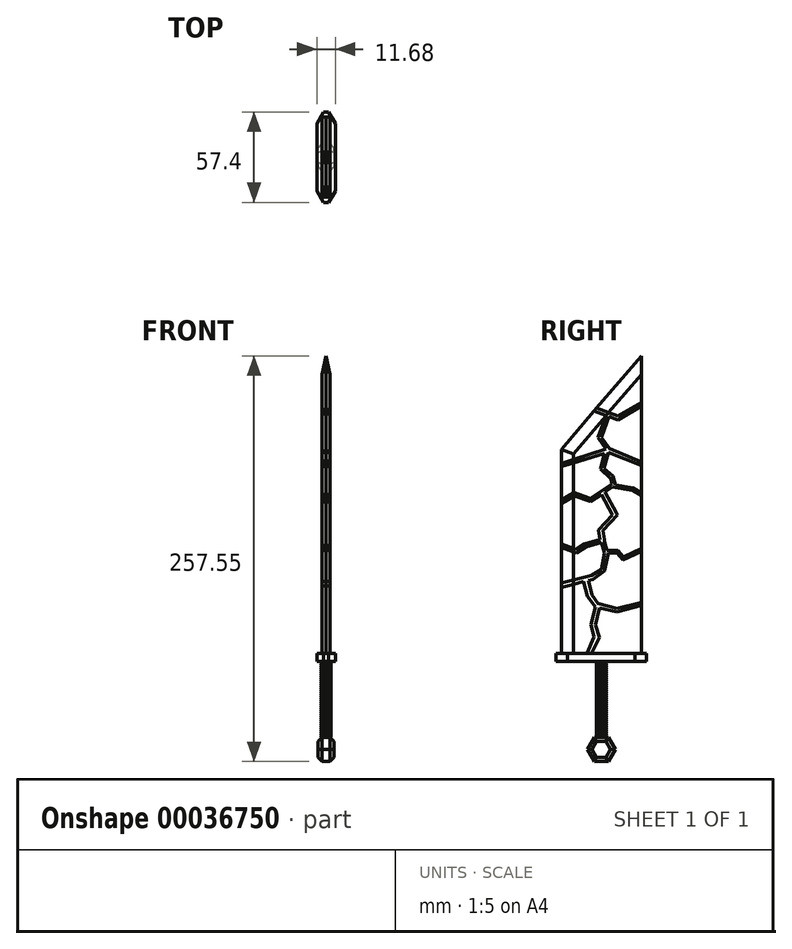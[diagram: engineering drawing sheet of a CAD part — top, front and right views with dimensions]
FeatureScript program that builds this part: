
annotation { "Feature Type Name" : "Feature", "Feature Type Description" : "" }
export const myFeature = defineFeature(function(context is Context, id is Id, definition is map)
    precondition{}
    {
        {
            var Q0;
            Q0=qCreatedBy(makeId("Right.planeOp"),FACE);
            var sketch = newSketch(context, id + "F0", { "sketchPlane" : qUnion([Q0])});
            skLineSegment(sketch, "E0", {"start": v(-25.4, 41.33) * mm, "end": v(-25.4, 83.27) * mm});
            skLineSegment(sketch, "E1", {"start": v(25.4, 41.33) * mm, "end": v(25.4, 71.64) * mm});
            skLineSegment(sketch, "E2", {"start": v(25.4, 171.08) * mm, "end": v(25.4, 198.27) * mm});
            skLineSegment(sketch, "E3", {"start": v(25.4, 230.2) * mm, "end": v(-2.99, 197.01) * mm});
            skLineSegment(sketch, "E4", {"start": v(25.4, 200.64) * mm, "end": v(10.42, 191.99) * mm});
            skLineSegment(sketch, "E5", {"start": v(25.4, 198.27) * mm, "end": v(10.42, 189.63) * mm});
            skLineSegment(sketch, "E6", {"start": v(10.42, 191.99) * mm, "end": v(-2.99, 197.01) * mm});
            skLineSegment(sketch, "E7", {"start": v(10.42, 189.63) * mm, "end": v(4.82, 191.68) * mm});
            skLineSegment(sketch, "E8.trimOffspring", {"start": v(-4.6, 195.13) * mm, "end": v(-25.4, 170.8) * mm});
            skLineSegment(sketch, "E9.trimOffspring", {"start": v(25.4, 200.64) * mm, "end": v(25.4, 230.2) * mm});
            skLineSegment(sketch, "E10", {"start": v(2.91, 192.38) * mm, "end": v(-2.2, 178.46) * mm});
            skLineSegment(sketch, "E11", {"start": v(-2.2, 178.46) * mm, "end": v(2.98, 171.03) * mm});
            skLineSegment(sketch, "E12", {"start": v(4.45, 168.92) * mm, "end": v(25.4, 160.6) * mm});
            skLineSegment(sketch, "E13", {"start": v(4.82, 191.68) * mm, "end": v(0, 178.53) * mm});
            skLineSegment(sketch, "E14", {"start": v(0, 178.53) * mm, "end": v(5, 171.35) * mm});
            skLineSegment(sketch, "E15", {"start": v(5, 171.35) * mm, "end": v(25.4, 162.82) * mm});
            skPoint(sketch, "E16.end.orphan", {"position": v(25.4, 162.82) * mm});
            skLineSegment(sketch, "E17.trimOffspring", {"start": v(25.4, 162.82) * mm, "end": v(25.4, 171.08) * mm});
            skLineSegment(sketch, "E18.trimOffspring", {"start": v(2.91, 192.38) * mm, "end": v(-4.6, 195.13) * mm});
            skLineSegment(sketch, "E19", {"start": v(1.83, 168.13) * mm, "end": v(-25.4, 159.9) * mm});
            skLineSegment(sketch, "E20", {"start": v(2.98, 171.03) * mm, "end": v(-25.4, 161.87) * mm});
            skLineSegment(sketch, "E21.trimOffspring", {"start": v(-25.4, 161.87) * mm, "end": v(-25.4, 170.8) * mm});
            skLineSegment(sketch, "E22", {"start": v(1.83, 168.13) * mm, "end": v(-0.65, 158.4) * mm});
            skLineSegment(sketch, "E23", {"start": v(-0.65, 158.4) * mm, "end": v(6.14, 152.23) * mm});
            skLineSegment(sketch, "E24", {"start": v(6.14, 152.23) * mm, "end": v(6.68, 148.9) * mm});
            skLineSegment(sketch, "E25", {"start": v(7, 146.87) * mm, "end": v(20.03, 144.9) * mm});
            skLineSegment(sketch, "E26", {"start": v(20.03, 144.9) * mm, "end": v(25.4, 141.55) * mm});
            skLineSegment(sketch, "E27", {"start": v(4.45, 168.92) * mm, "end": v(1.56, 158.78) * mm});
            skLineSegment(sketch, "E28", {"start": v(1.56, 158.78) * mm, "end": v(7.43, 153.9) * mm});
            skLineSegment(sketch, "E29", {"start": v(7.43, 153.9) * mm, "end": v(8.95, 148.23) * mm});
            skLineSegment(sketch, "E30", {"start": v(8.95, 148.23) * mm, "end": v(20.11, 146.47) * mm});
            skLineSegment(sketch, "E31", {"start": v(20.11, 146.47) * mm, "end": v(25.4, 143.2) * mm});
            skLineSegment(sketch, "E32.trimOffspring", {"start": v(25.4, 143.2) * mm, "end": v(25.4, 160.6) * mm});
            skLineSegment(sketch, "E33", {"start": v(7, 146.87) * mm, "end": v(2.24, 143.71) * mm});
            skLineSegment(sketch, "E34", {"start": v(-6.87, 137.68) * mm, "end": v(-17.21, 141.33) * mm});
            skLineSegment(sketch, "E35", {"start": v(-17.21, 141.33) * mm, "end": v(-25.4, 136.67) * mm});
            skLineSegment(sketch, "E36", {"start": v(6.68, 148.9) * mm, "end": v(-7.04, 139.82) * mm});
            skLineSegment(sketch, "E37", {"start": v(-7.04, 139.82) * mm, "end": v(-17.31, 143.56) * mm});
            skLineSegment(sketch, "E38", {"start": v(-17.31, 143.56) * mm, "end": v(-25.4, 138.7) * mm});
            skLineSegment(sketch, "E39.trimOffspring", {"start": v(-25.4, 138.7) * mm, "end": v(-25.4, 159.9) * mm});
            skLineSegment(sketch, "E40", {"start": v(-25.4, 41.33) * mm, "end": v(25.4, 41.33) * mm});
            skLineSegment(sketch, "E41", {"start": v(0.07, 142.27) * mm, "end": v(7.1, 129.29) * mm});
            skLineSegment(sketch, "E42", {"start": v(7.1, 129.29) * mm, "end": v(-1.77, 119.78) * mm});
            skLineSegment(sketch, "E43", {"start": v(-1.77, 119.78) * mm, "end": v(-0.97, 113.72) * mm});
            skLineSegment(sketch, "E44", {"start": v(-0.97, 113.72) * mm, "end": v(-10.63, 110.68) * mm});
            skLineSegment(sketch, "E45", {"start": v(-10.63, 110.68) * mm, "end": v(-16.14, 107.25) * mm});
            skLineSegment(sketch, "E46", {"start": v(-16.14, 107.25) * mm, "end": v(-25.4, 110.92) * mm});
            skLineSegment(sketch, "E47", {"start": v(2.24, 143.71) * mm, "end": v(9.57, 130.56) * mm});
            skLineSegment(sketch, "E48", {"start": v(9.57, 130.56) * mm, "end": v(10.37, 129.13) * mm});
            skLineSegment(sketch, "E49", {"start": v(10.37, 129.13) * mm, "end": v(1.03, 119.3) * mm});
            skLineSegment(sketch, "E50", {"start": v(1.03, 119.3) * mm, "end": v(1.99, 113.8) * mm});
            skLineSegment(sketch, "E51", {"start": v(1.99, 113.8) * mm, "end": v(1.99, 112.36) * mm});
            skLineSegment(sketch, "E52", {"start": v(0, 111.77) * mm, "end": v(-9.83, 108.85) * mm});
            skLineSegment(sketch, "E53", {"start": v(-9.83, 108.85) * mm, "end": v(-15.9, 105.17) * mm});
            skLineSegment(sketch, "E54", {"start": v(-15.9, 105.17) * mm, "end": v(-25.4, 108.45) * mm});
            skLineSegment(sketch, "E55", {"start": v(1.99, 112.36) * mm, "end": v(3.64, 106.8) * mm});
            skLineSegment(sketch, "E56", {"start": v(3.64, 106.8) * mm, "end": v(10.53, 106.8) * mm});
            skLineSegment(sketch, "E57", {"start": v(10.53, 106.8) * mm, "end": v(13.96, 102.7) * mm});
            skLineSegment(sketch, "E58", {"start": v(13.96, 102.7) * mm, "end": v(25.4, 107.97) * mm});
            skLineSegment(sketch, "E59", {"start": v(0, 111.77) * mm, "end": v(1.99, 105.08) * mm});
            skLineSegment(sketch, "E60", {"start": v(9.76, 105.08) * mm, "end": v(13.86, 100.53) * mm});
            skLineSegment(sketch, "E61", {"start": v(13.86, 100.53) * mm, "end": v(25.4, 105.97) * mm});
            skLineSegment(sketch, "E62.trimOffspring", {"start": v(-25.4, 110.92) * mm, "end": v(-25.4, 136.67) * mm});
            skLineSegment(sketch, "E63.trimOffspring", {"start": v(25.4, 107.97) * mm, "end": v(25.4, 141.55) * mm});
            skLineSegment(sketch, "E64.trimOffspring", {"start": v(0.07, 142.27) * mm, "end": v(-6.87, 137.68) * mm});
            skLineSegment(sketch, "E65", {"start": v(1.99, 105.08) * mm, "end": v(0, 94.48) * mm});
            skLineSegment(sketch, "E66", {"start": v(0, 94.48) * mm, "end": v(-6.17, 90.77) * mm});
            skLineSegment(sketch, "E67", {"start": v(-6.17, 90.77) * mm, "end": v(-25.4, 85.94) * mm});
            skLineSegment(sketch, "E68", {"start": v(4.63, 105.08) * mm, "end": v(1.99, 93.55) * mm});
            skLineSegment(sketch, "E69", {"start": v(1.99, 93.55) * mm, "end": v(-5.45, 88.3) * mm});
            skLineSegment(sketch, "E70", {"start": v(-5.45, 88.3) * mm, "end": v(-8.14, 87.63) * mm});
            skLineSegment(sketch, "E71", {"start": v(-11.26, 86.84) * mm, "end": v(-8.9, 77.54) * mm});
            skLineSegment(sketch, "E72", {"start": v(-8.9, 77.54) * mm, "end": v(-3.9, 70.92) * mm});
            skLineSegment(sketch, "E73", {"start": v(-1.28, 70.3) * mm, "end": v(9.87, 67.63) * mm});
            skLineSegment(sketch, "E74", {"start": v(9.87, 67.63) * mm, "end": v(25.4, 71.64) * mm});
            skLineSegment(sketch, "E75", {"start": v(-8.14, 87.63) * mm, "end": v(-5.84, 78.54) * mm});
            skLineSegment(sketch, "E76", {"start": v(-5.84, 78.54) * mm, "end": v(-2.06, 73.08) * mm});
            skLineSegment(sketch, "E77", {"start": v(-2.06, 73.08) * mm, "end": v(9.77, 69.7) * mm});
            skLineSegment(sketch, "E78", {"start": v(9.77, 69.7) * mm, "end": v(25.4, 73.65) * mm});
            skLineSegment(sketch, "E79.trimOffspring", {"start": v(-11.26, 86.84) * mm, "end": v(-25.4, 83.27) * mm});
            skLineSegment(sketch, "E80.trimOffspring", {"start": v(-25.4, 85.94) * mm, "end": v(-25.4, 108.45) * mm});
            skLineSegment(sketch, "E81.trimOffspring", {"start": v(25.4, 73.65) * mm, "end": v(25.4, 105.97) * mm});
            skLineSegment(sketch, "E82", {"start": v(4.63, 105.08) * mm, "end": v(9.76, 105.08) * mm});
            skLineSegment(sketch, "E83", {"start": v(-3.9, 70.92) * mm, "end": v(-6.61, 59.6) * mm});
            skLineSegment(sketch, "E84", {"start": v(-6.61, 59.6) * mm, "end": v(-4.58, 51.74) * mm});
            skLineSegment(sketch, "E85", {"start": v(-4.58, 51.74) * mm, "end": v(-9.16, 41.33) * mm});
            skLineSegment(sketch, "E86", {"start": v(-1.28, 70.3) * mm, "end": v(-3.87, 59.47) * mm});
            skLineSegment(sketch, "E87", {"start": v(-3.87, 59.47) * mm, "end": v(-1.11, 51.4) * mm});
            skLineSegment(sketch, "E88", {"start": v(-1.11, 51.4) * mm, "end": v(-6.37, 41.33) * mm});
            skSolve(sketch);
        }
        {
            var Q0;
            Q0 = qSketchRegion(id + "F0", true);
            extrude(context, id + "F1", {"entities" : qUnion([Q0]), "endBound" : BoundingType.SYMMETRIC, "depth" : 5.08 * mm});
        }
        {
            var Q0;
            Q0=qCreatedBy(makeId("Right.planeOp"),FACE);
            var sketch = newSketch(context, id + "F2", { "sketchPlane" : qUnion([Q0])});
            skLineSegment(sketch, "E89.0", {"start": v(2.91, 192.38) * mm, "end": v(-4.6, 195.13) * mm});
            skLineSegment(sketch, "E90.0", {"start": v(10.42, 191.99) * mm, "end": v(-2.99, 197.01) * mm});
            skLineSegment(sketch, "E91.0", {"start": v(10.42, 189.63) * mm, "end": v(4.82, 191.68) * mm});
            skLineSegment(sketch, "E92.0", {"start": v(25.4, 198.27) * mm, "end": v(10.42, 189.63) * mm});
            skLineSegment(sketch, "E93.0", {"start": v(25.4, 200.64) * mm, "end": v(10.42, 191.99) * mm});
            skLineSegment(sketch, "E94.0", {"start": v(4.82, 191.68) * mm, "end": v(0, 178.53) * mm});
            skLineSegment(sketch, "E95.0", {"start": v(2.91, 192.38) * mm, "end": v(-2.2, 178.46) * mm});
            skLineSegment(sketch, "E96.0", {"start": v(-2.2, 178.46) * mm, "end": v(2.98, 171.03) * mm});
            skLineSegment(sketch, "E97.0", {"start": v(0, 178.53) * mm, "end": v(5, 171.35) * mm});
            skLineSegment(sketch, "E98.0", {"start": v(5, 171.35) * mm, "end": v(25.4, 162.82) * mm});
            skLineSegment(sketch, "E99.0", {"start": v(4.45, 168.92) * mm, "end": v(25.4, 160.6) * mm});
            skLineSegment(sketch, "E100.0", {"start": v(2.98, 171.03) * mm, "end": v(-25.4, 161.87) * mm});
            skLineSegment(sketch, "E101.0", {"start": v(1.83, 168.13) * mm, "end": v(-0.65, 158.4) * mm});
            skLineSegment(sketch, "E102.0", {"start": v(4.45, 168.92) * mm, "end": v(1.56, 158.78) * mm});
            skLineSegment(sketch, "E103.0", {"start": v(-0.65, 158.4) * mm, "end": v(6.14, 152.23) * mm});
            skLineSegment(sketch, "E104.0", {"start": v(1.56, 158.78) * mm, "end": v(7.43, 153.9) * mm});
            skLineSegment(sketch, "E105.0", {"start": v(7.43, 153.9) * mm, "end": v(8.95, 148.23) * mm});
            skLineSegment(sketch, "E106.0", {"start": v(6.14, 152.23) * mm, "end": v(6.68, 148.9) * mm});
            skLineSegment(sketch, "E107.0", {"start": v(8.95, 148.23) * mm, "end": v(20.11, 146.47) * mm});
            skLineSegment(sketch, "E108.0", {"start": v(20.11, 146.47) * mm, "end": v(25.4, 143.2) * mm});
            skLineSegment(sketch, "E109.0", {"start": v(20.03, 144.9) * mm, "end": v(25.4, 141.55) * mm});
            skLineSegment(sketch, "E110.0", {"start": v(7, 146.87) * mm, "end": v(20.03, 144.9) * mm});
            skLineSegment(sketch, "E111.0", {"start": v(6.68, 148.9) * mm, "end": v(-7.04, 139.82) * mm});
            skLineSegment(sketch, "E112.0", {"start": v(7, 146.87) * mm, "end": v(2.24, 143.71) * mm});
            skLineSegment(sketch, "E113.0", {"start": v(-17.31, 143.56) * mm, "end": v(-25.4, 138.7) * mm});
            skLineSegment(sketch, "E114.0", {"start": v(-17.21, 141.33) * mm, "end": v(-25.4, 136.67) * mm});
            skLineSegment(sketch, "E115.0", {"start": v(-7.04, 139.82) * mm, "end": v(-17.31, 143.56) * mm});
            skLineSegment(sketch, "E116.0", {"start": v(-6.87, 137.68) * mm, "end": v(-17.21, 141.33) * mm});
            skLineSegment(sketch, "E117.0", {"start": v(0.07, 142.27) * mm, "end": v(-6.87, 137.68) * mm});
            skLineSegment(sketch, "E118.0", {"start": v(0.07, 142.27) * mm, "end": v(7.1, 129.29) * mm});
            skLineSegment(sketch, "E119.0", {"start": v(2.24, 143.71) * mm, "end": v(9.57, 130.56) * mm});
            skLineSegment(sketch, "E120.0", {"start": v(9.57, 130.56) * mm, "end": v(10.37, 129.13) * mm});
            skLineSegment(sketch, "E121.0", {"start": v(10.37, 129.13) * mm, "end": v(1.03, 119.3) * mm});
            skLineSegment(sketch, "E122.0", {"start": v(7.1, 129.29) * mm, "end": v(-1.77, 119.78) * mm});
            skLineSegment(sketch, "E123.0", {"start": v(-1.77, 119.78) * mm, "end": v(-0.97, 113.72) * mm});
            skLineSegment(sketch, "E124.0", {"start": v(1.03, 119.3) * mm, "end": v(1.99, 113.8) * mm});
            skLineSegment(sketch, "E125.0", {"start": v(1.99, 113.8) * mm, "end": v(1.99, 112.36) * mm});
            skLineSegment(sketch, "E126.0", {"start": v(1.99, 112.36) * mm, "end": v(3.64, 106.8) * mm});
            skLineSegment(sketch, "E127.0", {"start": v(0, 111.77) * mm, "end": v(1.99, 105.08) * mm});
            skLineSegment(sketch, "E128.0", {"start": v(-0.97, 113.72) * mm, "end": v(-10.63, 110.68) * mm});
            skLineSegment(sketch, "E129.0", {"start": v(-10.63, 110.68) * mm, "end": v(-16.14, 107.25) * mm});
            skLineSegment(sketch, "E130.0", {"start": v(-16.14, 107.25) * mm, "end": v(-25.4, 110.92) * mm});
            skLineSegment(sketch, "E131.0", {"start": v(-15.9, 105.17) * mm, "end": v(-25.4, 108.45) * mm});
            skLineSegment(sketch, "E132.0", {"start": v(-9.83, 108.85) * mm, "end": v(-15.9, 105.17) * mm});
            skLineSegment(sketch, "E133.0", {"start": v(0, 111.77) * mm, "end": v(-9.83, 108.85) * mm});
            skLineSegment(sketch, "E134.0", {"start": v(3.64, 106.8) * mm, "end": v(10.53, 106.8) * mm});
            skLineSegment(sketch, "E135.0", {"start": v(4.63, 105.08) * mm, "end": v(9.76, 105.08) * mm});
            skLineSegment(sketch, "E136.0", {"start": v(9.76, 105.08) * mm, "end": v(13.86, 100.53) * mm});
            skLineSegment(sketch, "E137.0", {"start": v(10.53, 106.8) * mm, "end": v(13.96, 102.7) * mm});
            skLineSegment(sketch, "E138.0", {"start": v(13.96, 102.7) * mm, "end": v(25.4, 107.97) * mm});
            skLineSegment(sketch, "E139.0", {"start": v(13.86, 100.53) * mm, "end": v(25.4, 105.97) * mm});
            skLineSegment(sketch, "E140.0", {"start": v(1.99, 105.08) * mm, "end": v(0, 94.48) * mm});
            skLineSegment(sketch, "E141.0", {"start": v(4.63, 105.08) * mm, "end": v(1.99, 93.55) * mm});
            skLineSegment(sketch, "E142.0", {"start": v(0, 94.48) * mm, "end": v(-6.17, 90.77) * mm});
            skLineSegment(sketch, "E143.0", {"start": v(-6.17, 90.77) * mm, "end": v(-25.4, 85.94) * mm});
            skLineSegment(sketch, "E144.0", {"start": v(1.99, 93.55) * mm, "end": v(-5.45, 88.3) * mm});
            skLineSegment(sketch, "E145.0", {"start": v(-5.45, 88.3) * mm, "end": v(-8.14, 87.63) * mm});
            skLineSegment(sketch, "E146.0", {"start": v(-11.26, 86.84) * mm, "end": v(-25.4, 83.27) * mm});
            skLineSegment(sketch, "E147.0", {"start": v(-11.26, 86.84) * mm, "end": v(-8.9, 77.54) * mm});
            skLineSegment(sketch, "E148.0", {"start": v(-8.14, 87.63) * mm, "end": v(-5.84, 78.54) * mm});
            skLineSegment(sketch, "E149.0", {"start": v(-5.84, 78.54) * mm, "end": v(-2.06, 73.08) * mm});
            skLineSegment(sketch, "E150.0", {"start": v(-8.9, 77.54) * mm, "end": v(-3.9, 70.92) * mm});
            skLineSegment(sketch, "E151.0", {"start": v(-2.06, 73.08) * mm, "end": v(9.77, 69.7) * mm});
            skLineSegment(sketch, "E152.0", {"start": v(9.77, 69.7) * mm, "end": v(25.4, 73.65) * mm});
            skLineSegment(sketch, "E153.0", {"start": v(9.87, 67.63) * mm, "end": v(25.4, 71.64) * mm});
            skLineSegment(sketch, "E154.0", {"start": v(-1.28, 70.3) * mm, "end": v(9.87, 67.63) * mm});
            skLineSegment(sketch, "E155.0", {"start": v(-3.9, 70.92) * mm, "end": v(-6.61, 59.6) * mm});
            skLineSegment(sketch, "E156.0", {"start": v(-1.28, 70.3) * mm, "end": v(-3.87, 59.47) * mm});
            skLineSegment(sketch, "E157.0", {"start": v(-3.87, 59.47) * mm, "end": v(-1.11, 51.4) * mm});
            skLineSegment(sketch, "E158.0", {"start": v(-6.61, 59.6) * mm, "end": v(-4.58, 51.74) * mm});
            skLineSegment(sketch, "E159.0", {"start": v(-1.11, 51.4) * mm, "end": v(-6.37, 41.33) * mm});
            skLineSegment(sketch, "E160.0", {"start": v(-4.58, 51.74) * mm, "end": v(-9.16, 41.33) * mm});
            skLineSegment(sketch, "E161", {"start": v(-9.16, 41.33) * mm, "end": v(-6.37, 41.33) * mm});
            skLineSegment(sketch, "E162", {"start": v(-25.4, 85.94) * mm, "end": v(-25.4, 83.27) * mm});
            skLineSegment(sketch, "E163", {"start": v(-25.4, 108.45) * mm, "end": v(-25.4, 110.92) * mm});
            skLineSegment(sketch, "E164", {"start": v(-25.4, 138.7) * mm, "end": v(-25.4, 136.67) * mm});
            skLineSegment(sketch, "E165", {"start": v(-25.4, 161.87) * mm, "end": v(-25.4, 159.92) * mm});
            skLineSegment(sketch, "E166", {"start": v(-25.4, 159.92) * mm, "end": v(-25.4, 161.87) * mm});
            skLineSegment(sketch, "E167", {"start": v(-4.6, 195.13) * mm, "end": v(-2.99, 197.01) * mm});
            skLineSegment(sketch, "E168", {"start": v(25.4, 198.27) * mm, "end": v(25.4, 200.64) * mm});
            skLineSegment(sketch, "E169", {"start": v(25.4, 162.82) * mm, "end": v(25.4, 160.6) * mm});
            skLineSegment(sketch, "E170", {"start": v(25.4, 143.2) * mm, "end": v(25.4, 141.55) * mm});
            skLineSegment(sketch, "E171", {"start": v(25.4, 107.97) * mm, "end": v(25.4, 105.97) * mm});
            skLineSegment(sketch, "E172", {"start": v(25.4, 73.65) * mm, "end": v(25.4, 71.64) * mm});
            skLineSegment(sketch, "E173", {"start": v(-25.4, 161.87) * mm, "end": v(2.98, 171.03) * mm});
            skLineSegment(sketch, "E174", {"start": v(-25.4, 159.92) * mm, "end": v(1.83, 168.13) * mm});
            skSolve(sketch);
        }
        {
            var Q0;
            Q0 = qSketchRegion(id + "F2", true);
            extrude(context, id + "F3", {"entities" : qUnion([Q0]), "endBound" : BoundingType.SYMMETRIC, "depth" : 5.08 * mm});
        }
        {
            var Q0;
            Q0=makeQuery(id+"F1.opExtrude","CAP_EDGE",EDGE,{"disambiguationData":[OSD([sQuery(id+"F0.wireOp",EDGE,"E8.trimOffspring")])],"isStart":true});
            var Q1;
            Q1=makeQuery(id+"F1.opExtrude","CAP_EDGE",EDGE,{"disambiguationData":[OSD([sQuery(id+"F0.wireOp",EDGE,"E8.trimOffspring")])],"isStart":false});
            var Q2;
            Q2=makeQuery(id+"F1.opExtrude","CAP_EDGE",EDGE,{"disambiguationData":[OSD([sQuery(id+"F0.wireOp",EDGE,"E39.trimOffspring")])],"isStart":false});
            var Q3;
            Q3=makeQuery(id+"F1.opExtrude","CAP_EDGE",EDGE,{"disambiguationData":[OSD([sQuery(id+"F0.wireOp",EDGE,"E39.trimOffspring")])],"isStart":true});
            var Q4;
            Q4=makeQuery(id+"F1.opExtrude","CAP_EDGE",EDGE,{"disambiguationData":[OSD([sQuery(id+"F0.wireOp",EDGE,"E21.trimOffspring")])],"isStart":true});
            var Q5;
            Q5=makeQuery(id+"F1.opExtrude","CAP_EDGE",EDGE,{"disambiguationData":[OSD([sQuery(id+"F0.wireOp",EDGE,"E21.trimOffspring")])],"isStart":false});
            var Q6;
            Q6=makeQuery(id+"F1.opExtrude","CAP_EDGE",EDGE,{"disambiguationData":[OSD([sQuery(id+"F0.wireOp",EDGE,"E62.trimOffspring")])],"isStart":false});
            var Q7;
            Q7=makeQuery(id+"F1.opExtrude","CAP_EDGE",EDGE,{"disambiguationData":[OSD([sQuery(id+"F0.wireOp",EDGE,"E62.trimOffspring")])],"isStart":true});
            var Q8;
            Q8=makeQuery(id+"F1.opExtrude","CAP_EDGE",EDGE,{"disambiguationData":[OSD([sQuery(id+"F0.wireOp",EDGE,"E80.trimOffspring")])],"isStart":false});
            var Q9;
            Q9=makeQuery(id+"F1.opExtrude","CAP_EDGE",EDGE,{"disambiguationData":[OSD([sQuery(id+"F0.wireOp",EDGE,"E80.trimOffspring")])],"isStart":true});
            var Q10;
            Q10=makeQuery(id+"F1.opExtrude","CAP_EDGE",EDGE,{"disambiguationData":[OSD([sQuery(id+"F0.wireOp",EDGE,"E0")])],"isStart":false});
            var Q11;
            Q11=makeQuery(id+"F1.opExtrude","CAP_EDGE",EDGE,{"disambiguationData":[OSD([sQuery(id+"F0.wireOp",EDGE,"E0")])],"isStart":true});
            var Q12;
            Q12=makeQuery(id+"F3.opExtrude","CAP_EDGE",EDGE,{"disambiguationData":[OSD([sQuery(id+"F2.wireOp",EDGE,"E162")])],"isStart":true});
            var Q13;
            Q13=makeQuery(id+"F3.opExtrude","CAP_EDGE",EDGE,{"disambiguationData":[OSD([sQuery(id+"F2.wireOp",EDGE,"E162")])],"isStart":false});
            var Q14;
            Q14=makeQuery(id+"F3.opExtrude","CAP_EDGE",EDGE,{"disambiguationData":[OSD([sQuery(id+"F2.wireOp",EDGE,"E163")])],"isStart":false});
            var Q15;
            Q15=makeQuery(id+"F3.opExtrude","CAP_EDGE",EDGE,{"disambiguationData":[OSD([sQuery(id+"F2.wireOp",EDGE,"E163")])],"isStart":true});
            var Q16;
            Q16=makeQuery(id+"F3.opExtrude","CAP_EDGE",EDGE,{"disambiguationData":[OSD([sQuery(id+"F2.wireOp",EDGE,"E164")])],"isStart":true});
            var Q17;
            Q17=makeQuery(id+"F3.opExtrude","CAP_EDGE",EDGE,{"disambiguationData":[OSD([sQuery(id+"F2.wireOp",EDGE,"E166")])],"isStart":false});
            var Q18;
            Q18=makeQuery(id+"F3.opExtrude","CAP_EDGE",EDGE,{"disambiguationData":[OSD([sQuery(id+"F2.wireOp",EDGE,"E166")])],"isStart":true});
            var Q19;
            Q19=makeQuery(id+"F1.opExtrude","CAP_EDGE",EDGE,{"disambiguationData":[OSD([sQuery(id+"F0.wireOp",EDGE,"E3")])],"isStart":true});
            var Q20;
            Q20=makeQuery(id+"F1.opExtrude","CAP_EDGE",EDGE,{"disambiguationData":[OSD([sQuery(id+"F0.wireOp",EDGE,"E3")])],"isStart":false});
            var Q21;
            Q21=makeQuery(id+"F3.opExtrude","CAP_EDGE",EDGE,{"disambiguationData":[OSD([sQuery(id+"F2.wireOp",EDGE,"E167")])],"isStart":false});
            var Q22;
            Q22=makeQuery(id+"F3.opExtrude","CAP_EDGE",EDGE,{"disambiguationData":[OSD([sQuery(id+"F2.wireOp",EDGE,"E167")])],"isStart":true});
            chamfer(context, id + "F4", {"entities" : qUnion([Q0, Q1, Q2, Q3, Q4, Q5, Q6, Q7, Q8, Q9, Q10, Q11, Q12, Q13, Q14, Q15, Q16, Q17, Q18, Q19, Q20, Q21, Q22]), "chamferType" : ChamferType.TWO_OFFSETS, "width1" : 2.54 * mm, "oppositeDirection" : false, "width2" : 7.62 * mm, "tangentPropagation" : true});
        }
        {
            var Q0;
            Q0=makeQuery(id+"F3.opExtrude","CAP_EDGE",EDGE,{"disambiguationData":[OSD([sQuery(id+"F2.wireOp",EDGE,"E164")])],"isStart":false});
            chamfer(context, id + "F5", {"entities" : qUnion([Q0]), "chamferType" : ChamferType.TWO_OFFSETS, "width1" : 7.62 * mm, "oppositeDirection" : false, "width2" : 2.54 * mm, "tangentPropagation" : true});
        }
        {
            var Q0;
            {var subQ0=sQuery(id+"F0.wireOp",EDGE,"E40");Q0=makeQuery(id+"F1.opExtrude","SWEPT_FACE",FACE,{"disambiguationData":[OSD([subQ0]),TDD([makeQuery(id+"F0.imprint","IMPRINT",EDGE,{"disambiguationData":[TD([[makeQuery(id+"F0.imprint","INTERSECT",VERTEX,{"derivedFrom":[sQuery(id+"F0.wireOp",EDGE,"E1"),subQ0]}),1.0]])],"derivedFrom":subQ0})])]});}
            var sketch = newSketch(context, id + "F6", { "sketchPlane" : qUnion([Q0])});
            skLineSegment(sketch, "E175.rect.bottom", {"start": v(-1.63, 28.7) * mm, "end": v(1.63, 28.7) * mm});
            skLineSegment(sketch, "E175.rect.top", {"start": v(-1.63, -28.7) * mm, "end": v(1.63, -28.7) * mm});
            skLineSegment(sketch, "E175.rect.left", {"start": v(-5.84, 21.4) * mm, "end": v(-5.84, -21.4) * mm});
            skLineSegment(sketch, "E175.rect.right", {"start": v(5.84, 21.4) * mm, "end": v(5.84, -21.4) * mm});
            skPoint(sketch, "E175.rect.middle", {"position": v(0, 0) * mm});
            skLineSegment(sketch, "E176", {"start": v(-5.84, 28.7) * mm, "end": v(-2.68, 26.88) * mm});
            skLineSegment(sketch, "E177", {"start": v(0, 0) * mm, "end": v(-3.69, 0) * mm});
            skLineSegment(sketch, "E178", {"start": v(-3.69, 0) * mm, "end": v(0, 0) * mm});
            skLineSegment(sketch, "E179", {"start": v(0, 0) * mm, "end": v(0, 2.62) * mm});
            skLineSegment(sketch, "E180.MirrorCS", {"start": v(5.84, 28.7) * mm, "end": v(2.68, 26.88) * mm});
            skLineSegment(sketch, "E181.MirrorCS", {"start": v(-5.84, -28.7) * mm, "end": v(-2.68, -26.88) * mm});
            skLineSegment(sketch, "E182.MirrorCS", {"start": v(5.84, -28.7) * mm, "end": v(2.68, -26.88) * mm});
            skLineSegment(sketch, "E183", {"start": v(-2.68, -26.88) * mm, "end": v(-5.84, -21.4) * mm});
            skLineSegment(sketch, "E184", {"start": v(-2.68, -26.88) * mm, "end": v(-1.63, -28.7) * mm});
            skLineSegment(sketch, "E185", {"start": v(2.68, -26.88) * mm, "end": v(1.63, -28.7) * mm});
            skLineSegment(sketch, "E186", {"start": v(2.68, -26.88) * mm, "end": v(5.84, -21.4) * mm});
            skLineSegment(sketch, "E187.MirrorCS", {"start": v(-2.68, 26.88) * mm, "end": v(-5.84, 21.4) * mm});
            skLineSegment(sketch, "E188.MirrorCS", {"start": v(2.68, 26.88) * mm, "end": v(1.63, 28.7) * mm});
            skLineSegment(sketch, "E189.MirrorCS", {"start": v(2.68, 26.88) * mm, "end": v(5.84, 21.4) * mm});
            skLineSegment(sketch, "E190.MirrorCS", {"start": v(-2.68, 26.88) * mm, "end": v(-1.63, 28.7) * mm});
            skPoint(sketch, "E191.orphan", {"position": v(5.84, 28.7) * mm});
            skPoint(sketch, "E192.orphan", {"position": v(5.84, -28.7) * mm});
            skPoint(sketch, "E193.orphan", {"position": v(-5.84, -28.7) * mm});
            skSolve(sketch);
        }
        {
            var Q0;
            Q0 = qSketchRegion(id + "F6", true);
            extrude(context, id + "F7", {"entities" : qUnion([Q0]), "depth" : 5.08 * mm});
        }
        {
            var Q0;
            Q0=makeQuery(id+"F7.opExtrude","CAP_FACE",FACE,{"disambiguationData":[OSD([sQuery(id+"F6.wireOp",EDGE,"E175.rect.bottom"),sQuery(id+"F6.wireOp",EDGE,"E175.rect.top"),sQuery(id+"F6.wireOp",EDGE,"E175.rect.left"),sQuery(id+"F6.wireOp",EDGE,"E175.rect.right"),sQuery(id+"F6.wireOp",EDGE,"E183"),sQuery(id+"F6.wireOp",EDGE,"E184"),sQuery(id+"F6.wireOp",EDGE,"E185"),sQuery(id+"F6.wireOp",EDGE,"E186"),sQuery(id+"F6.wireOp",EDGE,"E187.MirrorCS"),sQuery(id+"F6.wireOp",EDGE,"E188.MirrorCS"),sQuery(id+"F6.wireOp",EDGE,"E189.MirrorCS"),sQuery(id+"F6.wireOp",EDGE,"E190.MirrorCS")])],"isStart":false});
            var sketch = newSketch(context, id + "F8", { "sketchPlane" : qUnion([Q0])});
            skCircle(sketch, "E194", {"center": v(0, 0) * mm, "radius": 2.54 * mm});
            skSolve(sketch);
        }
        {
            var Q0;
            Q0=qCreatedBy(makeId("Right.planeOp"),FACE);
            var sketch = newSketch(context, id + "F9", { "sketchPlane" : qUnion([Q0])});
            skLineSegment(sketch, "E195.0", {"start": v(2.54, -15.28) * mm, "end": v(-2.54, -15.28) * mm});
            skLineSegment(sketch, "E196", {"start": v(0, -15.28) * mm, "end": v(0, -19.68) * mm});
            skCircle(sketch, "E197.cCircle", {"center": v(0, -19.68) * mm, "radius": 5.08 * mm, "construction": true});
            skLineSegment(sketch, "E197.0", {"start": v(-2.54, -15.28) * mm, "end": v(2.54, -15.28) * mm});
            skArc(sketch, "E198.cCircle", {"start": v(4.4, -17.14) * mm, "mid": v(-4.9, -21) * mm, "end": v(5.08, -19.68) * mm, "construction": true});
            skLineSegment(sketch, "E198.1", {"start": v(2.54, -15.28) * mm, "end": v(5.08, -19.68) * mm});
            skLineSegment(sketch, "E198.2", {"start": v(5.08, -19.68) * mm, "end": v(-1.45, -31) * mm});
            skLineSegment(sketch, "E198.3", {"start": v(2.54, -24.08) * mm, "end": v(-2.54, -24.08) * mm});
            skLineSegment(sketch, "E198.4", {"start": v(-2.54, -24.08) * mm, "end": v(-5.08, -19.68) * mm});
            skPoint(sketch, "E199.orphan", {"position": v(4.9, -21) * mm});
            skPoint(sketch, "E200.orphan", {"position": v(-4.4, -22.22) * mm});
            skLineSegment(sketch, "E201", {"start": v(2.54, -24.08) * mm, "end": v(-1.45, -31) * mm});
            skCircle(sketch, "E202.cCircle", {"center": v(0, -19.68) * mm, "radius": 7.67 * mm, "construction": true});
            skLineSegment(sketch, "E202.0", {"start": v(-4.43, -12.01) * mm, "end": v(4.43, -12.01) * mm});
            skLineSegment(sketch, "E202.1", {"start": v(4.43, -12.01) * mm, "end": v(8.86, -19.68) * mm});
            skLineSegment(sketch, "E202.2", {"start": v(8.86, -19.68) * mm, "end": v(4.43, -27.35) * mm});
            skLineSegment(sketch, "E202.3", {"start": v(4.43, -27.35) * mm, "end": v(-4.43, -27.35) * mm});
            skLineSegment(sketch, "E202.4", {"start": v(-4.43, -27.35) * mm, "end": v(-8.86, -19.68) * mm});
            skLineSegment(sketch, "E202.5", {"start": v(-8.86, -19.68) * mm, "end": v(-4.43, -12.01) * mm});
            skPoint(sketch, "E202.0.midPoint", {"position": v(0, -12.01) * mm});
            skLineSegment(sketch, "E203.0", {"start": v(-21.4, 36.25) * mm, "end": v(21.4, 36.25) * mm});
            skSolve(sketch);
        }
        {
            var Q0;
            Q0 = qSketchRegion(id + "F9", true);
            var Q1;
            {var subQ0=sQuery(id+"F9.wireOp",EDGE,"E198.1");Q1=makeQuery(id+"F9.imprint","IMPRINT",FACE,{"disambiguationData":[TD([[makeQuery(id+"F9.imprint","IMPRINT",EDGE,{"derivedFrom":subQ0}),-1.0]])]});}
            extrude(context, id + "F10", {"entities" : qUnion([Q0, Q1]), "endBound" : BoundingType.SYMMETRIC, "depth" : 10.16 * mm});
        }
        {
            var Q0;
            Q0=makeQuery(id+"F10.opExtrude","CAP_EDGE",EDGE,{"disambiguationData":[OSD([sQuery(id+"F9.wireOp",EDGE,"E202.0")])],"isStart":false});
            var Q1;
            Q1=makeQuery(id+"F10.opExtrude","CAP_FACE",FACE,{"disambiguationData":[OSD([sQuery(id+"F9.wireOp",EDGE,"E202.0"),sQuery(id+"F9.wireOp",EDGE,"E202.1"),sQuery(id+"F9.wireOp",EDGE,"E202.2"),sQuery(id+"F9.wireOp",EDGE,"E202.3"),sQuery(id+"F9.wireOp",EDGE,"E202.4"),sQuery(id+"F9.wireOp",EDGE,"E202.5")])],"isStart":false});
            var Q2;
            Q2=makeQuery(id+"F10.opExtrude","CAP_FACE",FACE,{"disambiguationData":[OSD([sQuery(id+"F9.wireOp",EDGE,"E202.0"),sQuery(id+"F9.wireOp",EDGE,"E202.1"),sQuery(id+"F9.wireOp",EDGE,"E202.2"),sQuery(id+"F9.wireOp",EDGE,"E202.3"),sQuery(id+"F9.wireOp",EDGE,"E202.4"),sQuery(id+"F9.wireOp",EDGE,"E202.5")])],"isStart":true});
            chamfer(context, id + "F11", {"entities" : qUnion([Q0, Q1, Q2]), "width" : 2.54 * mm, "tangentPropagation" : true});
        }
        {
            var Q0;
            Q0 = qSketchRegion(id + "F8", true);
            extrude(context, id + "F12", {"entities" : qUnion([Q0]), "depth" : 48.26 * mm});
        }
        {
            var Q0;
            Q0=qCreatedBy(makeId("Right.planeOp"),FACE);
            var sketch = newSketch(context, id + "F13", { "sketchPlane" : qUnion([Q0])});
            skLineSegment(sketch, "E204", {"start": v(-2.54, -11.28) * mm, "end": v(-2.54, 36.25) * mm});
            skLineSegment(sketch, "E205", {"start": v(2.54, 36.25) * mm, "end": v(2.54, -11.28) * mm});
            skArc(sketch, "E206", {"start": v(-2.54, 36.25) * mm, "mid": v(-3.18, 35.61) * mm, "end": v(-2.54, 34.98) * mm});
            skLineSegment(sketch, "E207.0", {"start": v(-21.4, 36.25) * mm, "end": v(21.4, 36.25) * mm});
            skArc(sketch, "E208.1.0.0", {"start": v(-2.54, 34.98) * mm, "mid": v(-3.18, 34.34) * mm, "end": v(-2.54, 33.7) * mm});
            skCircle(sketch, "E208.2.0.0", {"center": v(-2.54, 33.07) * mm, "radius": 0.64 * mm});
            skArc(sketch, "E208.3.0.0", {"start": v(-2.54, 32.44) * mm, "mid": v(-3.18, 31.8) * mm, "end": v(-2.54, 31.17) * mm});
            skArc(sketch, "E208.4.0.0", {"start": v(-2.54, 31.17) * mm, "mid": v(-3.18, 30.53) * mm, "end": v(-2.54, 29.9) * mm});
            skArc(sketch, "E208.5.0.0", {"start": v(-2.54, 29.9) * mm, "mid": v(-3.18, 29.26) * mm, "end": v(-2.54, 28.63) * mm});
            skArc(sketch, "E208.6.0.0", {"start": v(-2.54, 28.63) * mm, "mid": v(-3.18, 28) * mm, "end": v(-2.54, 27.36) * mm});
            skArc(sketch, "E208.7.0.0", {"start": v(-2.54, 27.36) * mm, "mid": v(-3.18, 26.72) * mm, "end": v(-2.54, 26.09) * mm});
            skArc(sketch, "E208.8.0.0", {"start": v(-2.54, 26.09) * mm, "mid": v(-3.18, 25.45) * mm, "end": v(-2.54, 24.82) * mm});
            skArc(sketch, "E208.9.0.0", {"start": v(-2.54, 24.82) * mm, "mid": v(-3.18, 24.18) * mm, "end": v(-2.54, 23.55) * mm});
            skLineSegment(sketch, "E208.direction1", {"start": v(-2.54, 35.61) * mm, "end": v(-2.54, 34.34) * mm, "construction": true});
            skArc(sketch, "E209.0.10.0", {"start": v(-2.54, 23.55) * mm, "mid": v(-3.18, 22.91) * mm, "end": v(-2.54, 22.28) * mm});
            skArc(sketch, "E209.0.11.0", {"start": v(-2.54, 22.28) * mm, "mid": v(-3.18, 21.64) * mm, "end": v(-2.54, 21) * mm});
            skArc(sketch, "E209.0.12.0", {"start": v(-2.54, 21) * mm, "mid": v(-3.18, 20.37) * mm, "end": v(-2.54, 19.74) * mm});
            skCircle(sketch, "E209.0.13.0", {"center": v(-2.54, 19.1) * mm, "radius": 0.64 * mm});
            skCircle(sketch, "E209.0.14.0", {"center": v(-2.54, 17.83) * mm, "radius": 0.64 * mm});
            skCircle(sketch, "E209.0.15.0", {"center": v(-2.54, 16.56) * mm, "radius": 0.64 * mm});
            skCircle(sketch, "E209.0.16.0", {"center": v(-2.54, 15.3) * mm, "radius": 0.64 * mm});
            skCircle(sketch, "E209.0.17.0", {"center": v(-2.54, 14.02) * mm, "radius": 0.64 * mm});
            skCircle(sketch, "E209.0.18.0", {"center": v(-2.54, 12.75) * mm, "radius": 0.64 * mm});
            skLineSegment(sketch, "E210", {"start": v(-2.54, 36.25) * mm, "end": v(-2.54, 12.12) * mm});
            skLineSegment(sketch, "E211", {"start": v(0, 0) * mm, "end": v(0, 10.88) * mm});
            skArc(sketch, "E212.0.19.0", {"start": v(-2.54, 12.12) * mm, "mid": v(-3.18, 11.48) * mm, "end": v(-2.54, 10.85) * mm});
            skArc(sketch, "E212.0.20.0", {"start": v(-2.54, 10.85) * mm, "mid": v(-3.18, 10.21) * mm, "end": v(-2.54, 9.58) * mm});
            skArc(sketch, "E212.0.21.0", {"start": v(-2.54, 9.58) * mm, "mid": v(-3.18, 8.94) * mm, "end": v(-2.54, 8.3) * mm});
            skArc(sketch, "E212.0.22.0", {"start": v(-2.54, 8.3) * mm, "mid": v(-3.18, 7.67) * mm, "end": v(-2.54, 7.04) * mm});
            skArc(sketch, "E212.0.23.0", {"start": v(-2.54, 7.04) * mm, "mid": v(-3.18, 6.4) * mm, "end": v(-2.54, 5.77) * mm});
            skArc(sketch, "E212.0.24.0", {"start": v(-2.54, 5.77) * mm, "mid": v(-3.18, 5.13) * mm, "end": v(-2.54, 4.5) * mm});
            skArc(sketch, "E212.0.25.0", {"start": v(-2.54, 4.5) * mm, "mid": v(-3.18, 3.86) * mm, "end": v(-2.54, 3.23) * mm});
            skArc(sketch, "E212.0.26.0", {"start": v(-2.54, 3.23) * mm, "mid": v(-3.18, 2.6) * mm, "end": v(-2.54, 1.96) * mm});
            skArc(sketch, "E212.0.27.0", {"start": v(-2.54, 1.96) * mm, "mid": v(-3.18, 1.32) * mm, "end": v(-2.54, 0.69) * mm});
            skArc(sketch, "E212.0.28.0", {"start": v(-2.54, 0.69) * mm, "mid": v(-3.17, 0.05) * mm, "end": v(-2.54, -0.58) * mm});
            skArc(sketch, "E212.0.29.0", {"start": v(-2.54, -0.58) * mm, "mid": v(-3.17, -1.22) * mm, "end": v(-2.54, -1.85) * mm});
            skArc(sketch, "E212.0.30.0", {"start": v(-2.54, -1.85) * mm, "mid": v(-3.17, -2.49) * mm, "end": v(-2.54, -3.12) * mm});
            skArc(sketch, "E212.0.31.0", {"start": v(-2.54, -3.12) * mm, "mid": v(-3.17, -3.76) * mm, "end": v(-2.54, -4.4) * mm});
            skArc(sketch, "E212.0.32.0", {"start": v(-2.54, -4.4) * mm, "mid": v(-3.17, -5.03) * mm, "end": v(-2.54, -5.66) * mm});
            skArc(sketch, "E212.0.33.0", {"start": v(-2.54, -5.66) * mm, "mid": v(-3.17, -6.3) * mm, "end": v(-2.54, -6.93) * mm});
            skArc(sketch, "E212.0.34.0", {"start": v(-2.54, -6.93) * mm, "mid": v(-3.17, -7.57) * mm, "end": v(-2.54, -8.2) * mm});
            skArc(sketch, "E212.0.35.0", {"start": v(-2.54, -8.2) * mm, "mid": v(-3.17, -8.84) * mm, "end": v(-2.54, -9.47) * mm});
            skArc(sketch, "E212.0.36.0", {"start": v(-2.54, -9.47) * mm, "mid": v(-3.17, -10.1) * mm, "end": v(-2.54, -10.74) * mm});
            skArc(sketch, "E212.0.37.0", {"start": v(-2.54, -10.74) * mm, "mid": v(-3.17, -11.38) * mm, "end": v(-2.54, -12.01) * mm});
            skLineSegment(sketch, "E213", {"start": v(-2.54, -6.93) * mm, "end": v(-2.54, -12.01) * mm});
            skSolve(sketch);
        }
        {
            var Q0;
            Q0 = qSketchRegion(id + "F13", true);
            var Q1;
            Q1=sQuery(id+"F13.wireOp",EDGE,"E211");
            revolve(context, id + "F14", {"operationType" : NewBodyOperationType.ADD, "entities" : qUnion([Q0]), "axis" : qUnion([Q1]), "revolveType" : RevolveType.FULL});
        }
    });
